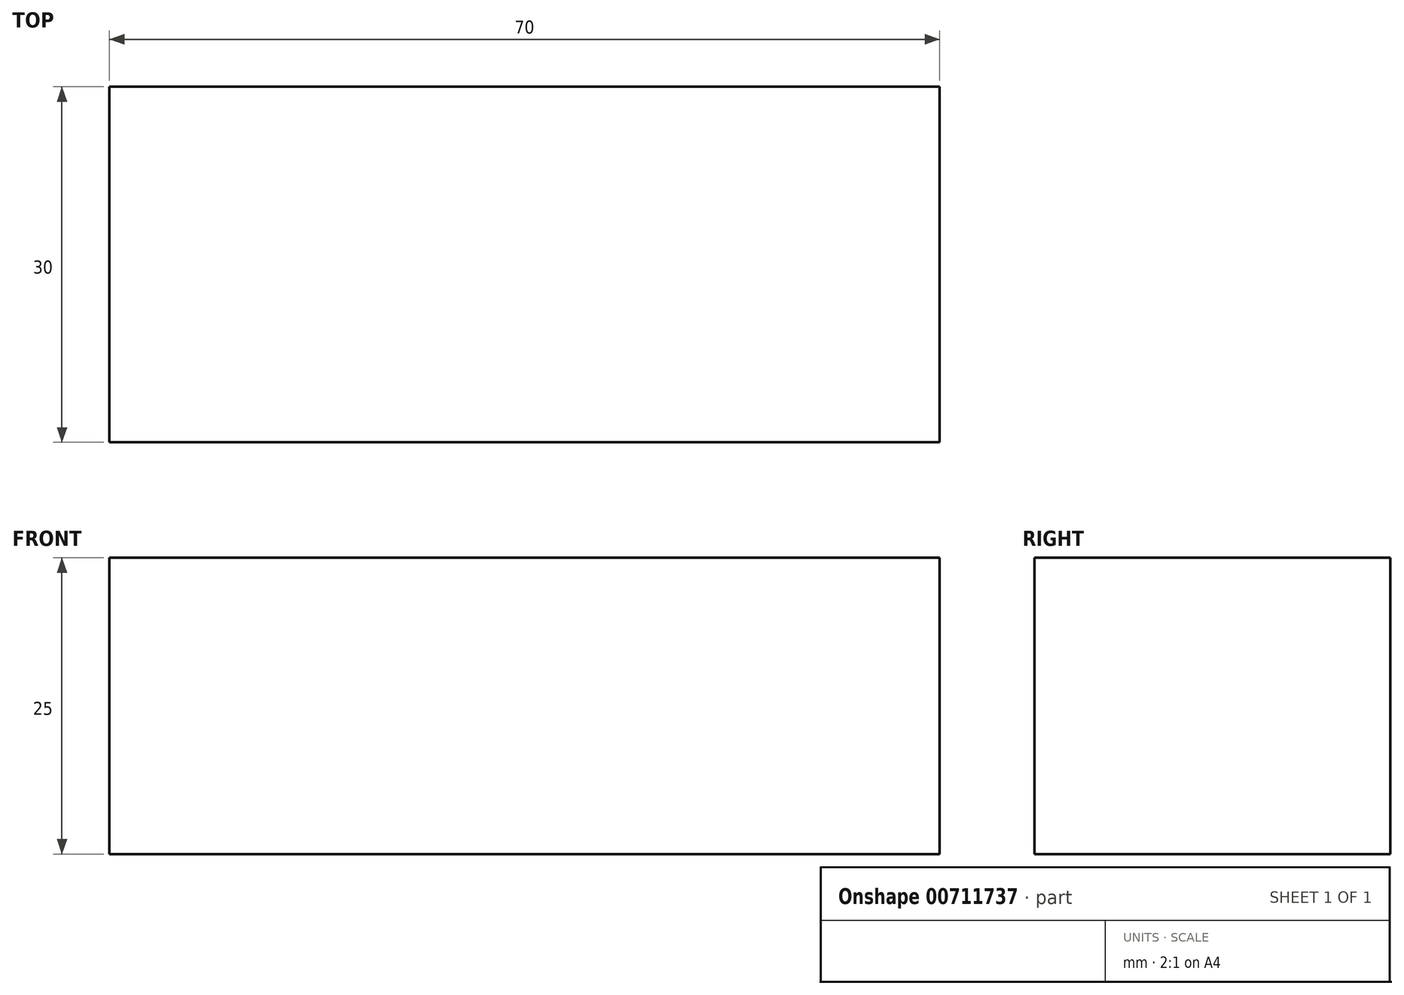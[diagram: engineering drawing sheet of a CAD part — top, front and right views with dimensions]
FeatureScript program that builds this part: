
annotation { "Feature Type Name" : "Feature", "Feature Type Description" : "" }
export const myFeature = defineFeature(function(context is Context, id is Id, definition is map)
    precondition{}
    {
        {
            var Q0;
            Q0=qCreatedBy(makeId("Top.planeOp"),FACE);
            var sketch = newSketch(context, id + "F0", { "sketchPlane" : qUnion([Q0])});
            skLineSegment(sketch, "E0.bottom", {"start": v(-35, 15) * mm, "end": v(35, 15) * mm});
            skLineSegment(sketch, "E0.top", {"start": v(-35, -15) * mm, "end": v(35, -15) * mm});
            skLineSegment(sketch, "E0.left", {"start": v(-35, 15) * mm, "end": v(-35, -15) * mm});
            skLineSegment(sketch, "E0.right", {"start": v(35, 15) * mm, "end": v(35, -15) * mm});
            skPoint(sketch, "E0.middle", {"position": v(0, 0) * mm});
            skSolve(sketch);
        }
        {
            var Q0;
            Q0=makeQuery(id+"F0.imprint","IMPRINT",FACE,{"disambiguationData":[TD([[makeQuery(id+"F0.imprint","IMPRINT",EDGE,{"derivedFrom":sQuery(id+"F0.wireOp",EDGE,"E0.bottom")}),-1.0]])]});
            extrude(context, id + "F1", {"entities" : qUnion([Q0]), "depth" : 25 * mm, "offsetDistance" : 25 * mm});
        }
    });
